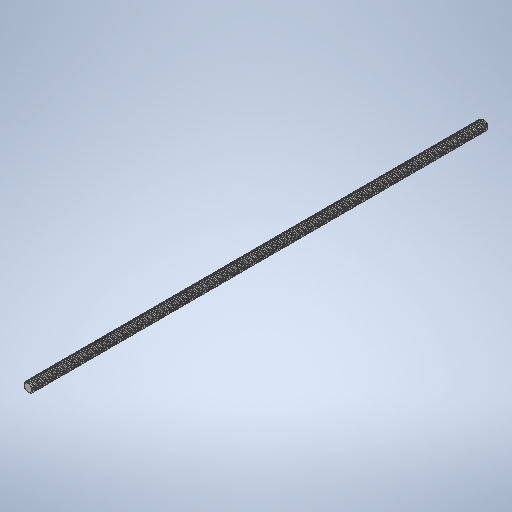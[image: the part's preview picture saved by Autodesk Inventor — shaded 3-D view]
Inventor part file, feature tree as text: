
AUTODESK INVENTOR PART (.ipt)
format: ipt  version: 2025.2 (Build 292293000, 293)  size: 1,654,784 bytes
history: native  units: mm
features: extrude x1, chamfer x1, other x1, pattern_circular x1
ambient origin geometry x8: Origin, YZ Plane, XZ Plane, XY Plane, X Axis, Y Axis, Z Axis, Center Point
bodies: Solid1 (feature_tree)
feature tree (4):
  extrude  "1000mm Rod"  Depth=380.0mm TaperAngle=0.0deg
  chamfer  "Chamfer1"  Distance=0.907143mm Angle=45.0deg
  other  "ACME Thread 2mm Pitch"
  pattern_circular  "4 Start"  [2 undecoded]
note: 2 required parameter values undecoded (feature->parameter linkage not recoverable at this tier; creation-order binding heuristic only, values carry confidence <= 0.55)
